# Revit family: Lavatory_System-Wall_Mount-Trueform_Concrete-Double_Ramp_Basin-Configurable_2_Station
name_source: partatom
category: Plumbing Fixtures
revit_build: Autodesk Revit LT 2015 (Build: 20140606_1530(x64)
units: mm (PartAtom-declared; Revit-internal decimal feet)

## types (6) — shared parameters
Additional Support Required Note = No
Basin Height = 5"
Basin/Countertop Reconciliation Warning = No
Bracket Placement Warning = No
Brackets = Steel, Paint Finish, Dark Gray, Matte
Description = Wall-mount GFRC Two Station Ramp Basin Lavatory
Lavatory = GFRC - Concrete
Left Bracket - L = No
Left Bracket - T = Yes
Manufacturer = Trueform Concrete
Non Standard Sink Basin Model Note = No
RLAC = 1/8"
RRAC = 1/8"
Remove Left Apron = No
Remove Right Apron = No
Right Bracket - L = No
Right Bracket - T = Yes
SDC = 1/4"
Tailpiece = Polished Chrome
URL = https://www.trueformconcrete.com
Use Left Bracket = Yes
Use Right Bracket = Yes
Vent Connection = No
Verify Rear Countertop = 5"
Waste Connection = Yes
Waste Fitting = 1 1/4"

## per-type parameters (varying)
- R-1812: AHC=5"; Apron Height=5"; BDC=17"; BSC=2"; Basin Center to Basin Center=30"; Basin Center to Basin Center MAX=36"; Basin Center to Basin Center MIN=21"; Basin Depth=12"; Basin Front Setback=2"; Basin Front Setback Max=5"; Basin ID (Do not edit value)=1812; Basin Length=18"; CWFU=0.5; HWFU=0.5; Left Bracket to Countertop Center=27"; Left Bracket to Countertop Center MAX=28 1/2"; Left Bracket to Countertop Center MIN=25 1/2"; Model=Custom Lavatory; ODC=19"; Overall Countertop Depth=19"; Overall Countertop Depth MIN=14"; Overall Countertop Length=60"; Overall Countertop Length MIN=45"; Right Bracket to Countertop Center=27"; Right Bracket to Countertop Center MAX=28 1/2"; Right Bracket to Countertop Center MIN=25 1/2"; Verify Basin Center to Basin Center=30"; Verify Basin Front Setback=2"; Verify Left Bracket Placement=27"; Verify Left and Right Countertop Lengths=6"; Verify Middle Countertop Length=12"; Verify Overall Countertop Depth=19"; Verify Overall Countertop Length=60"; Verify Right Bracket Placement=27"; WFU=1
- R-2013 (FLO-72V-DBL-ADA): AHC=5"; Apron Height=5"; BDC=19"; BSC=3"; Basin Center to Basin Center=36"; Basin Center to Basin Center MAX=46"; Basin Center to Basin Center MIN=23"; Basin Depth=13"; Basin Front Setback=3"; Basin Front Setback Max=6"; Basin ID (Do not edit value)=2013; Basin Length=20"; CWFU=1; HWFU=1; Left Bracket to Countertop Center=32"; Left Bracket to Countertop Center MAX=34 1/2"; Left Bracket to Countertop Center MIN=29 1/2"; Model=FLO-72V-DBL-ADA; ODC=21"; Overall Countertop Depth=21"; Overall Countertop Depth MIN=15"; Overall Countertop Length=72"; Overall Countertop Length MIN=49"; Right Bracket to Countertop Center=32"; Right Bracket to Countertop Center MAX=34 1/2"; Right Bracket to Countertop Center MIN=29 1/2"; Verify Basin Center to Basin Center=36"; Verify Basin Front Setback=3"; Verify Left Bracket Placement=32"; Verify Left and Right Countertop Lengths=8"; Verify Middle Countertop Length=16"; Verify Overall Countertop Depth=21"; Verify Overall Countertop Length=72"; Verify Right Bracket Placement=32"; WFU=2
- R-1410: AHC=5"; Apron Height=5"; BDC=15"; BSC=2"; Basin Center to Basin Center=30"; Basin Center to Basin Center MAX=40"; Basin Center to Basin Center MIN=17"; Basin Depth=10"; Basin Front Setback=2"; Basin Front Setback Max=5"; Basin ID (Do not edit value)=1410; Basin Length=14"; CWFU=0.5; HWFU=0.5; Left Bracket to Countertop Center=27"; Left Bracket to Countertop Center MAX=28 1/2"; Left Bracket to Countertop Center MIN=23 1/2"; Model=Custom Lavatory; ODC=17"; Overall Countertop Depth=17"; Overall Countertop Depth MIN=12"; Overall Countertop Length=60"; Overall Countertop Length MIN=37"; Right Bracket to Countertop Center=27"; Right Bracket to Countertop Center MAX=28 1/2"; Right Bracket to Countertop Center MIN=23 1/2"; Verify Basin Center to Basin Center=30"; Verify Basin Front Setback=2"; Verify Left Bracket Placement=27"; Verify Left and Right Countertop Lengths=8"; Verify Middle Countertop Length=16"; Verify Overall Countertop Depth=17"; Verify Overall Countertop Length=60"; Verify Right Bracket Placement=27"; WFU=1
- R-2013 (FLO-60V-DBL-ADA): AHC=5"; Apron Height=5"; BDC=19"; BSC=3"; Basin Center to Basin Center=30"; Basin Center to Basin Center MAX=34"; Basin Center to Basin Center MIN=23"; Basin Depth=13"; Basin Front Setback=3"; Basin Front Setback Max=6"; Basin ID (Do not edit value)=2013; Basin Length=20"; CWFU=1; HWFU=1; Left Bracket to Countertop Center=27"; Left Bracket to Countertop Center MAX=28 1/2"; Left Bracket to Countertop Center MIN=26 1/2"; Model=FLO-60V-DBL-ADA; ODC=21"; Overall Countertop Depth=21"; Overall Countertop Depth MIN=15"; Overall Countertop Length=60"; Overall Countertop Length MIN=49"; Right Bracket to Countertop Center=27"; Right Bracket to Countertop Center MAX=28 1/2"; Right Bracket to Countertop Center MIN=26 1/2"; Verify Basin Center to Basin Center=30"; Verify Basin Front Setback=3"; Verify Left Bracket Placement=27"; Verify Left and Right Countertop Lengths=5"; Verify Middle Countertop Length=10"; Verify Overall Countertop Depth=21"; Verify Overall Countertop Length=60"; Verify Right Bracket Placement=27"; WFU=2
- R-2013 (FLO-72V-DBL-CONTEMPO): AHC=3"; Apron Height=3"; BDC=16"; BSC=1/8"; Basin Center to Basin Center=36"; Basin Center to Basin Center MAX=46"; Basin Center to Basin Center MIN=23"; Basin Depth=13"; Basin Front Setback=0"; Basin Front Setback Max=3"; Basin ID (Do not edit value)=2013; Basin Length=20"; CWFU=1; HWFU=1; Left Bracket to Countertop Center=32"; Left Bracket to Countertop Center MAX=34 1/2"; Left Bracket to Countertop Center MIN=29 1/2"; Model=FLO-72V-DBL-CONTEMPO; ODC=18"; Overall Countertop Depth=18"; Overall Countertop Depth MIN=15"; Overall Countertop Length=72"; Overall Countertop Length MIN=49"; Right Bracket to Countertop Center=32"; Right Bracket to Countertop Center MAX=34 1/2"; Right Bracket to Countertop Center MIN=29 1/2"; Verify Basin Center to Basin Center=36"; Verify Basin Front Setback=0"; Verify Left Bracket Placement=32"; Verify Left and Right Countertop Lengths=8"; Verify Middle Countertop Length=16"; Verify Overall Countertop Depth=18"; Verify Overall Countertop Length=72"; Verify Right Bracket Placement=32"; WFU=2
- R-2013 (FLO-60V-DBL-CONTEMPO): AHC=3"; Apron Height=3"; BDC=16"; BSC=1/8"; Basin Center to Basin Center=30"; Basin Center to Basin Center MAX=34"; Basin Center to Basin Center MIN=23"; Basin Depth=13"; Basin Front Setback=0"; Basin Front Setback Max=3"; Basin ID (Do not edit value)=2013; Basin Length=20"; CWFU=1; HWFU=1; Left Bracket to Countertop Center=27"; Left Bracket to Countertop Center MAX=28 1/2"; Left Bracket to Countertop Center MIN=26 1/2"; Model=FLO-60V-DBL-CONTEMPO; ODC=18"; Overall Countertop Depth=18"; Overall Countertop Depth MIN=15"; Overall Countertop Length=60"; Overall Countertop Length MIN=49"; Right Bracket to Countertop Center=27"; Right Bracket to Countertop Center MAX=28 1/2"; Right Bracket to Countertop Center MIN=26 1/2"; Verify Basin Center to Basin Center=30"; Verify Basin Front Setback=0"; Verify Left Bracket Placement=27"; Verify Left and Right Countertop Lengths=5"; Verify Middle Countertop Length=10"; Verify Overall Countertop Depth=18"; Verify Overall Countertop Length=60"; Verify Right Bracket Placement=27"; WFU=2

## geometry (parser evidence)
native form markers: Sweep x5
no freeform markers — native parametric forms only
